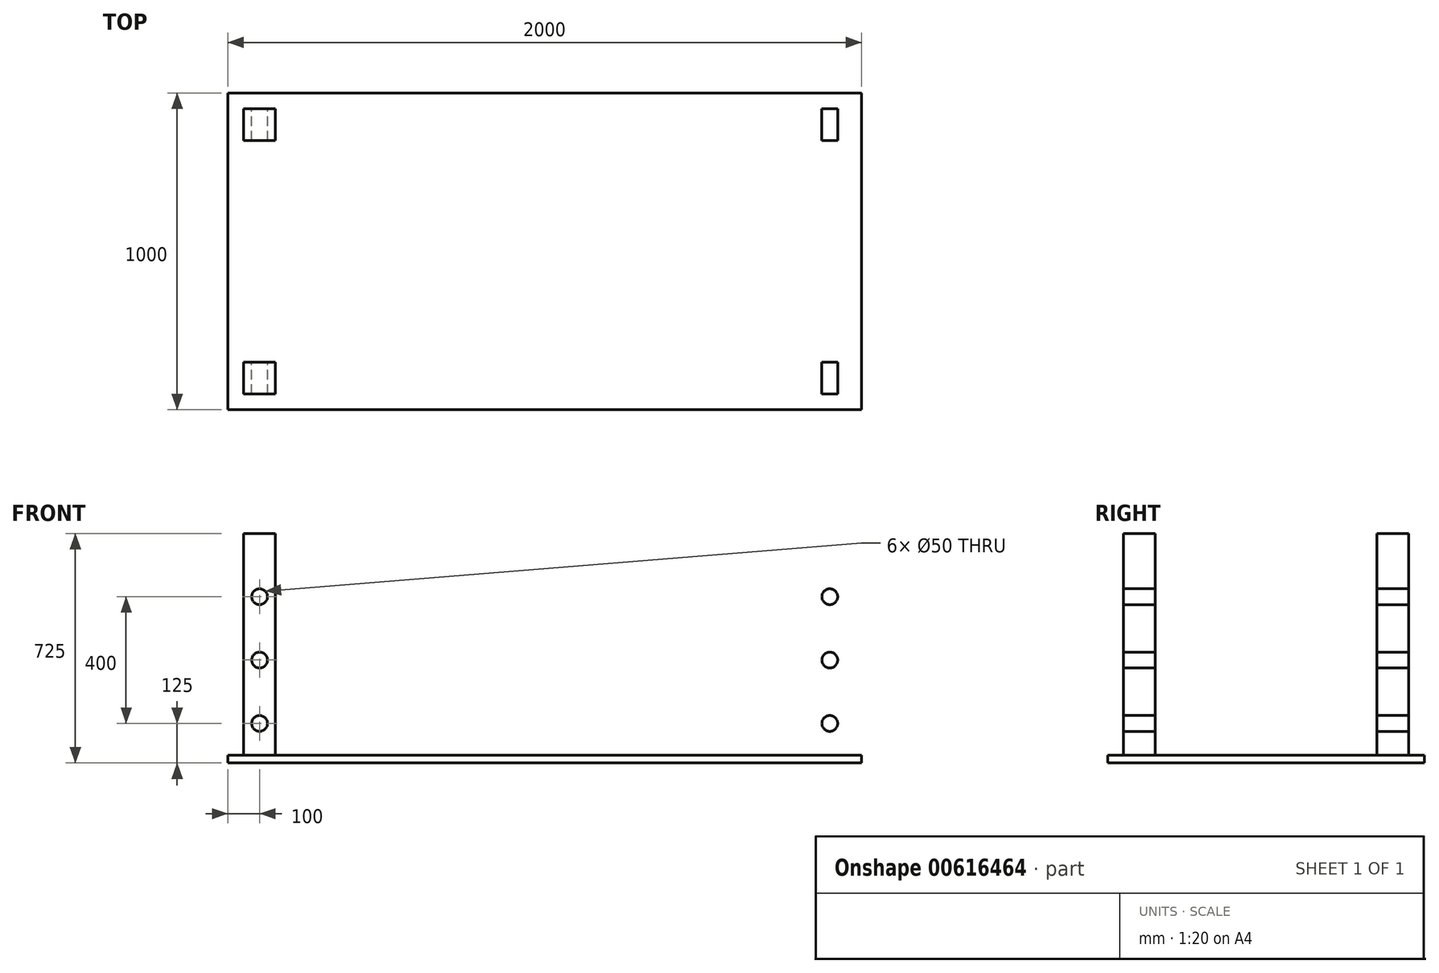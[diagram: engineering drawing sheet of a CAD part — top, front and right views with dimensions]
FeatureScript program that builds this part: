
annotation { "Feature Type Name" : "Feature", "Feature Type Description" : "" }
export const myFeature = defineFeature(function(context is Context, id is Id, definition is map)
    precondition{}
    {
        {
            var Q0;
            Q0=qCreatedBy(makeId("Top.planeOp"),FACE);
            var sketch = newSketch(context, id + "F0", { "sketchPlane" : qUnion([Q0])});
            skLineSegment(sketch, "E0.bottom", {"start": v(-1000, 500) * mm, "end": v(1000, 500) * mm});
            skLineSegment(sketch, "E0.top", {"start": v(-1000, -500) * mm, "end": v(1000, -500) * mm});
            skLineSegment(sketch, "E0.left", {"start": v(-1000, 500) * mm, "end": v(-1000, -500) * mm});
            skLineSegment(sketch, "E0.right", {"start": v(1000, 500) * mm, "end": v(1000, -500) * mm});
            skLineSegment(sketch, "E1", {"start": v(0, -500) * mm, "end": v(0, 500) * mm, "construction": true});
            skLineSegment(sketch, "E2", {"start": v(-1000, 0) * mm, "end": v(1000, 0) * mm, "construction": true});
            skSolve(sketch);
        }
        {
            var Q0;
            Q0=makeQuery(id+"F0.imprint","IMPRINT",FACE,{"disambiguationData":[TD([[makeQuery(id+"F0.imprint","IMPRINT",EDGE,{"derivedFrom":sQuery(id+"F0.wireOp",EDGE,"E0.bottom")}),-1.0]])]});
            extrude(context, id + "F1", {"entities" : qUnion([Q0]), "depth" : 25 * mm, "offsetDistance" : 25 * mm});
        }
        {
            var Q0;
            Q0=makeQuery(id+"F1.opExtrude","CAP_FACE",FACE,{"disambiguationData":[OSD([sQuery(id+"F0.wireOp",EDGE,"E0.bottom"),sQuery(id+"F0.wireOp",EDGE,"E0.top"),sQuery(id+"F0.wireOp",EDGE,"E0.left"),sQuery(id+"F0.wireOp",EDGE,"E0.right")])],"isStart":false});
            var sketch = newSketch(context, id + "F2", { "sketchPlane" : qUnion([Q0])});
            skLineSegment(sketch, "E3.bottom", {"start": v(-950, -450) * mm, "end": v(-850, -450) * mm});
            skLineSegment(sketch, "E3.top", {"start": v(-950, -350) * mm, "end": v(-850, -350) * mm});
            skLineSegment(sketch, "E3.left", {"start": v(-950, -450) * mm, "end": v(-950, -350) * mm});
            skLineSegment(sketch, "E3.right", {"start": v(-850, -450) * mm, "end": v(-850, -350) * mm});
            skLineSegment(sketch, "E4", {"start": v(0, -500) * mm, "end": v(0, 500) * mm, "construction": true});
            skLineSegment(sketch, "E5", {"start": v(-1000, 0) * mm, "end": v(1000, 0) * mm, "construction": true});
            skLineSegment(sketch, "E6.MirrorCS", {"start": v(950, -450) * mm, "end": v(950, -350) * mm});
            skLineSegment(sketch, "E7.MirrorCS", {"start": v(950, -450) * mm, "end": v(850, -450) * mm});
            skLineSegment(sketch, "E8.MirrorCS", {"start": v(850, -450) * mm, "end": v(850, -350) * mm});
            skLineSegment(sketch, "E9.MirrorCS", {"start": v(950, -350) * mm, "end": v(850, -350) * mm});
            skLineSegment(sketch, "E10.MirrorCS", {"start": v(850, 450) * mm, "end": v(850, 350) * mm});
            skLineSegment(sketch, "E11.MirrorCS", {"start": v(950, 450) * mm, "end": v(850, 450) * mm});
            skLineSegment(sketch, "E12.MirrorCS", {"start": v(950, 450) * mm, "end": v(950, 350) * mm});
            skLineSegment(sketch, "E13.MirrorCS", {"start": v(950, 350) * mm, "end": v(850, 350) * mm});
            skLineSegment(sketch, "E14.MirrorCS", {"start": v(-950, 350) * mm, "end": v(-850, 350) * mm});
            skLineSegment(sketch, "E15.MirrorCS", {"start": v(-950, 450) * mm, "end": v(-950, 350) * mm});
            skLineSegment(sketch, "E16.MirrorCS", {"start": v(-950, 450) * mm, "end": v(-850, 450) * mm});
            skLineSegment(sketch, "E17.MirrorCS", {"start": v(-850, 450) * mm, "end": v(-850, 350) * mm});
            skSolve(sketch);
        }
        {
            var Q0;
            Q0 = qSketchRegion(id + "F2", true);
            extrude(context, id + "F3", {"entities" : qUnion([Q0]), "operationType" : NewBodyOperationType.ADD, "depth" : 700 * mm, "offsetDistance" : 25 * mm});
        }
        {
            var Q0;
            Q0=makeQuery(id+"F3.opExtrude","SWEPT_FACE",FACE,{"disambiguationData":[OSD([sQuery(id+"F2.wireOp",EDGE,"E11.MirrorCS")])]});
            var sketch = newSketch(context, id + "F4", { "sketchPlane" : qUnion([Q0])});
            skCircle(sketch, "E18", {"center": v(900, 525) * mm, "radius": 25 * mm});
            skCircle(sketch, "E19", {"center": v(900, 325) * mm, "radius": 25 * mm});
            skCircle(sketch, "E20", {"center": v(900, 125) * mm, "radius": 25 * mm});
            skLineSegment(sketch, "E21", {"start": v(900, 725) * mm, "end": v(900, 25) * mm, "construction": true});
            skLineSegment(sketch, "E22", {"start": v(0, 0) * mm, "end": v(0, 794.13) * mm, "construction": true});
            skCircle(sketch, "E23.MirrorC", {"center": v(-900, 525) * mm, "radius": 25 * mm});
            skCircle(sketch, "E24.MirrorC", {"center": v(-900, 325) * mm, "radius": 25 * mm});
            skCircle(sketch, "E25.MirrorC", {"center": v(-900, 125) * mm, "radius": 25 * mm});
            skSolve(sketch);
        }
        {
            var Q0;
            Q0=makeQuery(id+"F4.imprint","IMPRINT",FACE,{"disambiguationData":[TD([[makeQuery(id+"F4.imprint","IMPRINT",EDGE,{"derivedFrom":sQuery(id+"F4.wireOp",EDGE,"E23.MirrorC")}),-1.0]])]});
            var Q1;
            Q1=makeQuery(id+"F4.imprint","IMPRINT",FACE,{"disambiguationData":[TD([[makeQuery(id+"F4.imprint","IMPRINT",EDGE,{"derivedFrom":sQuery(id+"F4.wireOp",EDGE,"E24.MirrorC")}),-1.0]])]});
            var Q2;
            Q2=makeQuery(id+"F4.imprint","IMPRINT",FACE,{"disambiguationData":[TD([[makeQuery(id+"F4.imprint","IMPRINT",EDGE,{"derivedFrom":sQuery(id+"F4.wireOp",EDGE,"E25.MirrorC")}),-1.0]])]});
            var Q3;
            Q3=makeQuery(id+"F4.imprint","IMPRINT",FACE,{"disambiguationData":[TD([[makeQuery(id+"F4.imprint","IMPRINT",EDGE,{"derivedFrom":sQuery(id+"F4.wireOp",EDGE,"E18")}),1.0]])]});
            var Q4;
            Q4=makeQuery(id+"F4.imprint","IMPRINT",FACE,{"disambiguationData":[TD([[makeQuery(id+"F4.imprint","IMPRINT",EDGE,{"derivedFrom":sQuery(id+"F4.wireOp",EDGE,"E19")}),1.0]])]});
            var Q5;
            Q5=makeQuery(id+"F4.imprint","IMPRINT",FACE,{"disambiguationData":[TD([[makeQuery(id+"F4.imprint","IMPRINT",EDGE,{"derivedFrom":sQuery(id+"F4.wireOp",EDGE,"E20")}),1.0]])]});
            extrude(context, id + "F5", {"entities" : qUnion([Q0, Q1, Q2, Q3, Q4, Q5]), "operationType" : NewBodyOperationType.REMOVE, "oppositeDirection" : true, "depth" : 900 * mm, "offsetDistance" : 25 * mm});
        }
    });
